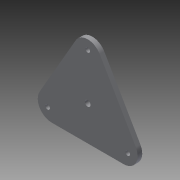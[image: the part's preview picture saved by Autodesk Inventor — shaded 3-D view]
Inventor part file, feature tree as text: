
AUTODESK INVENTOR PART (.ipt)
format: ipt  version: 2013 (Build 170138000, 138)  size: 90,112 bytes
history: native  units: in
note: dims shown in document units (in); Inventor stores cm internally (conversion verified against a paired STEP export)
features: extrude x1, fillet x1, sketch x1
ambient origin geometry x8: Origin, YZ Plane, XZ Plane, XY Plane, X Axis, Y Axis, Z Axis, Center Point
bodies: Solid1 (feature_tree)
feature tree (3):
  extrude  "Extrusion1"  Depth=0.25in
  fillet  "Fillet1"  Radius=2.5in
  sketch  "Sketch2"  dims[d0=0.3125in d1=0.25in d2=2.5in d3=1.1811in d5=360.0deg d8=0.5in d9=0.5in d10=0.5in d11=0.25in d12=0.0in d13=0.75in]
